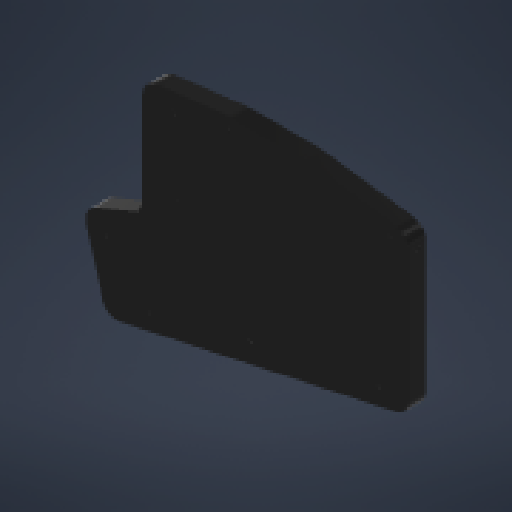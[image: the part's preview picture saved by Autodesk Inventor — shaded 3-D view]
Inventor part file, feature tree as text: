
AUTODESK INVENTOR PART (.ipt)
format: ipt  version: 2024.3 (Build 283343000, 343)  size: 581,120 bytes
history: native  units: in
note: dims shown in document units (in); Inventor stores cm internally (conversion verified against a paired STEP export)
features: extrude x9, sketch x9, projected_geometry x7, reference x5, other x4, fillet x2
ambient origin geometry x8: Origin, YZ Plane, XZ Plane, XY Plane, X Axis, Y Axis, Z Axis, Center Point
bodies: Solid1 (feature_tree)
feature tree (36):
  extrude  "Extrusion1"  Depth=0.125in TaperAngle=0.0deg
  extrude  "Extrusion2"  Depth=0.25in TaperAngle=0.0deg
  extrude  "Extrusion3"  Depth=0.125in
  extrude  "Extrusion7"  Depth=0.0312in
  extrude  "Extrusion8"  Depth=0.0312in
  fillet  "Fillet1"  Radius=0.0312in
  extrude  "Extrusion9"  Depth=0.0312in
  extrude  "Extrusion10"  Depth=0.125in
  extrude  "Extrusion11"  Depth=0.125in
  extrude  "Extrusion12"  Depth=0.125in
  fillet  "Fillet2"  Radius=0.125in
  sketch  "Sketch1"  dims[d0=0.125in d1=0.125in d2=0.0in]
  reference  "Reference1"
  sketch  "Sketch2"  dims[d3=0.12in d4=0.25in d5=0.0in]
  projected_geometry  "Projected Loop1"
  sketch  "Sketch3"  dims[d6=0.125in d7=0.0312in]
  reference  "Reference2"
  projected_geometry  "Projected Loop2"
  sketch  "Sketch7"  dims[d8=0.0312in d9=0.0312in]
  projected_geometry  "Projected Loop6"
  sketch  "Sketch8"  dims[d10=0.0312in d11=0.0312in d12=0.0312in]
  projected_geometry  "Projected Loop7"
  sketch  "Sketch9"  dims[d13=0.0312in d14=0.0312in]
  projected_geometry  "Projected Loop8"
  sketch  "Sketch10"  dims[d15=0.125in d16=0.125in]
  projected_geometry  "Projected Loop9"
  sketch  "Sketch11"  dims[d17=0.125in d18=0.125in]
  projected_geometry  "Projected Loop10"
  sketch  "Sketch12"  dims[d19=0.125in d20=0.125in d21=0.125in d22=0.125in d23=0.125in d24=0.125in d25=0.125in d26=0.125in d27=0.125in d28=0.125in d29=0.125in d30=0.0in d46=0.003in d47=0.003in d48=0.003in d49=0.003in d50=0.003in d51=0.003in d52=0.003in d53=0.003in d54=0.015in d55=0.25in d56=0.0in d57=0.125in d58=0.0in d59=0.75in d60=0.278in d61=0.0in d62=0.75in d63=0.278in d64=0.125in d65=0.0in d66=0.125in d67=0.153in d68=0.0765in d69=0.1875in d70=0.3in d71=0.0in d72=0.153in d73=0.0765in d74=0.1875in d75=0.3in d76=0.0in d77=0.153in d78=0.0765in d79=0.1875in d80=0.3in d81=0.0in d82=0.3in d83=0.0in d84=0.125in]
  reference  "Reference3"
  reference  "Reference4"
  reference  "Reference5"
  other  "<userpath>\Documents\GitHub\clackenPersonal\Case Cad\Main Case Assembly.iam"
  other  "Main Case Assembly.iam"
  other  "Split V2:1"
  other  "Top plate left:1"
